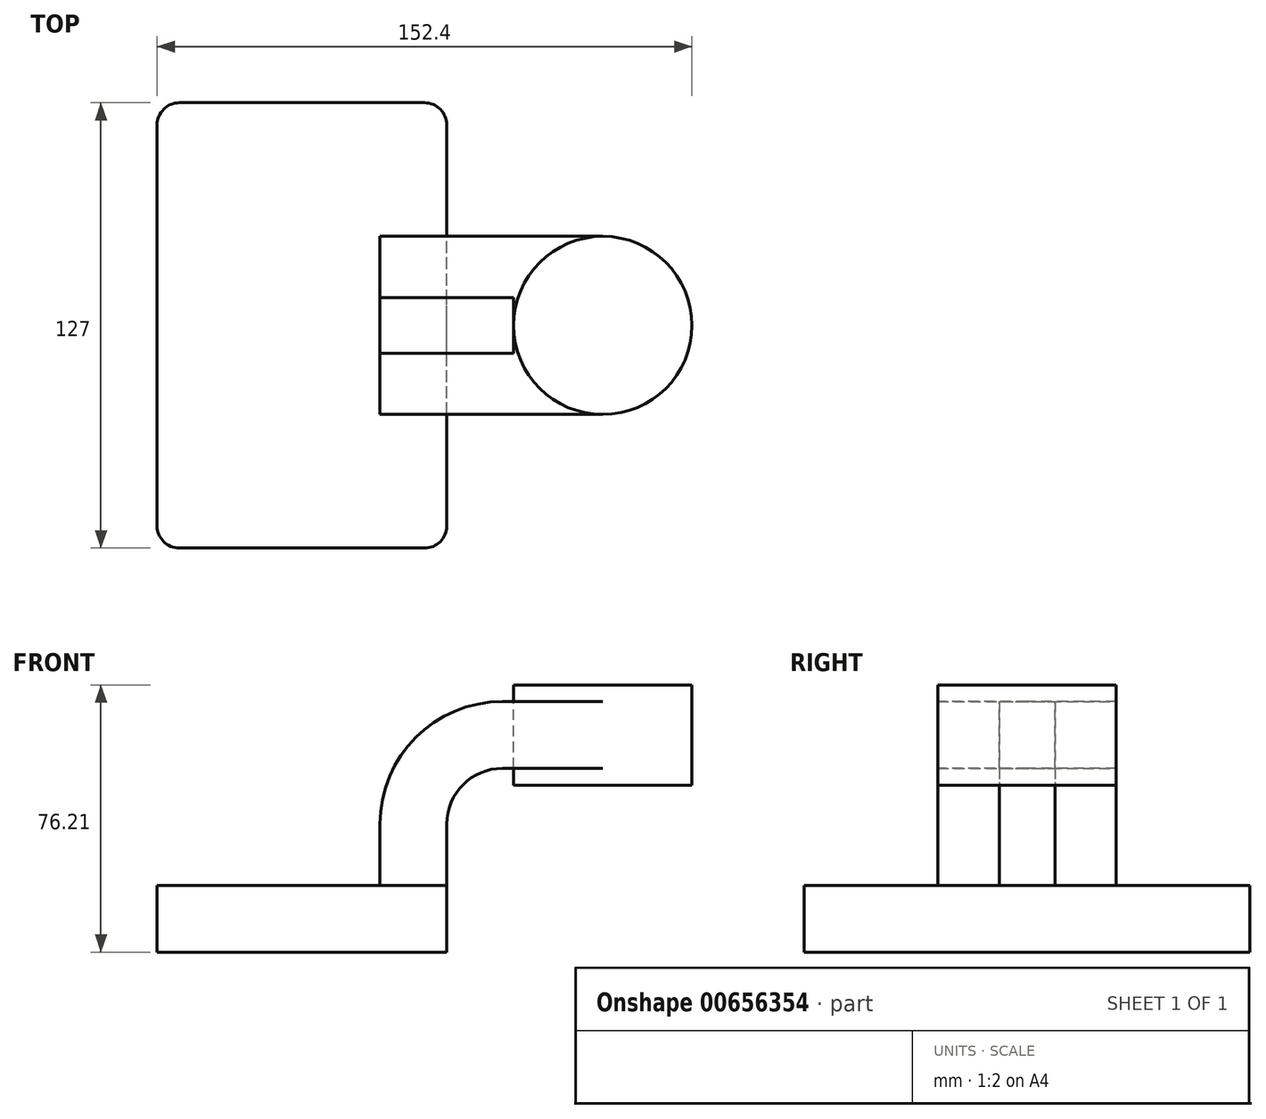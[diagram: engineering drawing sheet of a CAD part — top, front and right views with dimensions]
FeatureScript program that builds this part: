
annotation { "Feature Type Name" : "Feature", "Feature Type Description" : "" }
export const myFeature = defineFeature(function(context is Context, id is Id, definition is map)
    precondition{}
    {
        {
            var Q0;
            Q0=qCreatedBy(makeId("Front.planeOp"),FACE);
            var sketch = newSketch(context, id + "F0", { "sketchPlane" : qUnion([Q0])});
            skLineSegment(sketch, "E0.bottom", {"start": v(-41.28, -9.53) * mm, "end": v(41.28, -9.53) * mm});
            skLineSegment(sketch, "E0.top", {"start": v(-41.28, 9.53) * mm, "end": v(41.28, 9.53) * mm});
            skLineSegment(sketch, "E0.left", {"start": v(-41.28, -9.53) * mm, "end": v(-41.28, 9.53) * mm});
            skLineSegment(sketch, "E0.right", {"start": v(41.28, -9.53) * mm, "end": v(41.28, 9.53) * mm});
            skPoint(sketch, "E0.middle", {"position": v(0, 0) * mm});
            skLineSegment(sketch, "E1.bottom", {"start": v(111.12, 38.1) * mm, "end": v(60.32, 38.1) * mm});
            skLineSegment(sketch, "E1.top", {"start": v(111.12, 66.68) * mm, "end": v(60.32, 66.67) * mm});
            skLineSegment(sketch, "E1.left", {"start": v(111.12, 38.1) * mm, "end": v(111.12, 66.68) * mm});
            skLineSegment(sketch, "E1.right", {"start": v(60.32, 38.1) * mm, "end": v(60.32, 66.67) * mm});
            skPoint(sketch, "E1.middle", {"position": v(85.72, 52.39) * mm});
            skLineSegment(sketch, "E2", {"start": v(41.28, 9.52) * mm, "end": v(41.28, 27) * mm});
            skArc(sketch, "E3", {"start": v(41.27, 27) * mm, "mid": v(45.92, 38.23) * mm, "end": v(57.15, 42.88) * mm});
            skLineSegment(sketch, "E4", {"start": v(57.15, 42.88) * mm, "end": v(85.72, 42.88) * mm});
            skPoint(sketch, "E4.endSnap0", {"position": v(85.72, 38.1) * mm});
            skLineSegment(sketch, "E5.0", {"start": v(57.15, 61.93) * mm, "end": v(85.72, 61.93) * mm});
            skArc(sketch, "E5.1", {"start": v(22.22, 27) * mm, "mid": v(32.45, 51.7) * mm, "end": v(57.15, 61.93) * mm});
            skLineSegment(sketch, "E5.2", {"start": v(22.22, 9.52) * mm, "end": v(22.22, 27) * mm});
            skLineSegment(sketch, "E6", {"start": v(85.72, 38.1) * mm, "end": v(85.72, 66.67) * mm});
            skFitSpline(sketch, "E7", {"points": [v(-41.28, 9.53) * mm, v(57.15, 61.93) * mm], "startDerivative": vector(84.06, 137.11) * mm, "endDerivative": vector(99.62, -12.07) * mm});
            skSolve(sketch);
        }
        {
            var Q0;
            Q0=makeQuery(id+"F0.imprint","IMPRINT",FACE,{"disambiguationData":[TD([[makeQuery(id+"F0.imprint","IMPRINT",EDGE,{"derivedFrom":sQuery(id+"F0.wireOp",EDGE,"E0.bottom")}),1.0]])]});
            extrude(context, id + "F1", {"entities" : qUnion([Q0]), "endBound" : BoundingType.SYMMETRIC, "depth" : 127 * mm, "offsetDistance" : 25.4 * mm});
        }
        {
            var Q0;
            {var subQ1=sQuery(id+"F0.wireOp",EDGE,"E2");Q0=makeQuery(id+"F0.imprint","IMPRINT",FACE,{"disambiguationData":[TD([[makeQuery(id+"F0.imprint","IMPRINT",EDGE,{"derivedFrom":subQ1}),1.0]])]});}
            var Q1;
            {var subQ0=sQuery(id+"F0.wireOp",EDGE,"E4");var subQ1=sQuery(id+"F0.wireOp",EDGE,"E1.right");var subQ2=makeQuery(id+"F0.imprint","INTERSECT",VERTEX,{"derivedFrom":[subQ1,subQ0]});Q1=makeQuery(id+"F0.imprint","IMPRINT",FACE,{"disambiguationData":[TD([[makeQuery(id+"F0.imprint","IMPRINT",EDGE,{"disambiguationData":[TD([[subQ2,-1.0]])],"derivedFrom":subQ1}),-1.0]])]});}
            extrude(context, id + "F2", {"entities" : qUnion([Q0, Q1]), "endBound" : BoundingType.SYMMETRIC, "depth" : 50.8 * mm, "offsetDistance" : 25.4 * mm});
        }
        {
            var Q0;
            {var subQ4=sQuery(id+"F0.wireOp",EDGE,"E1.left");Q0=makeQuery(id+"F0.imprint","IMPRINT",FACE,{"disambiguationData":[TD([[makeQuery(id+"F0.imprint","IMPRINT",EDGE,{"derivedFrom":subQ4}),1.0]])]});}
            var Q1;
            Q1=sQuery(id+"F0.wireOp",EDGE,"E6");
            revolve(context, id + "F3", {"operationType" : NewBodyOperationType.ADD, "entities" : qUnion([Q0]), "axis" : qUnion([Q1]), "revolveType" : RevolveType.FULL});
        }
        {
            var Q0;
            Q0=makeQuery(id+"F1.opExtrude","CAP_EDGE",EDGE,{"disambiguationData":[OSD([sQuery(id+"F0.wireOp",EDGE,"E0.right")])],"isStart":false});
            var Q1;
            Q1=makeQuery(id+"F1.opExtrude","CAP_EDGE",EDGE,{"disambiguationData":[OSD([sQuery(id+"F0.wireOp",EDGE,"E0.left")])],"isStart":false});
            var Q2;
            Q2=makeQuery(id+"F1.opExtrude","CAP_EDGE",EDGE,{"disambiguationData":[OSD([sQuery(id+"F0.wireOp",EDGE,"E0.right")])],"isStart":true});
            var Q3;
            Q3=makeQuery(id+"F1.opExtrude","CAP_EDGE",EDGE,{"disambiguationData":[OSD([sQuery(id+"F0.wireOp",EDGE,"E0.left")])],"isStart":true});
            fillet(context, id + "F4", {"entities" : qUnion([Q0, Q1, Q2, Q3]), "radius" : 6.35 * mm, "tangentPropagation" : true, "allowEdgeOverflow" : false});
        }
        {
            var Q0;
            Q0=makeQuery(id+"F0.imprint","IMPRINT",FACE,{"disambiguationData":[TD([[makeQuery(id+"F0.imprint","IMPRINT",EDGE,{"derivedFrom":sQuery(id+"F0.wireOp",EDGE,"E5.1")}),1.0]])]});
            extrude(context, id + "F5", {"entities" : qUnion([Q0]), "endBound" : BoundingType.SYMMETRIC, "depth" : 15.88 * mm, "offsetDistance" : 25.4 * mm});
        }
    });
